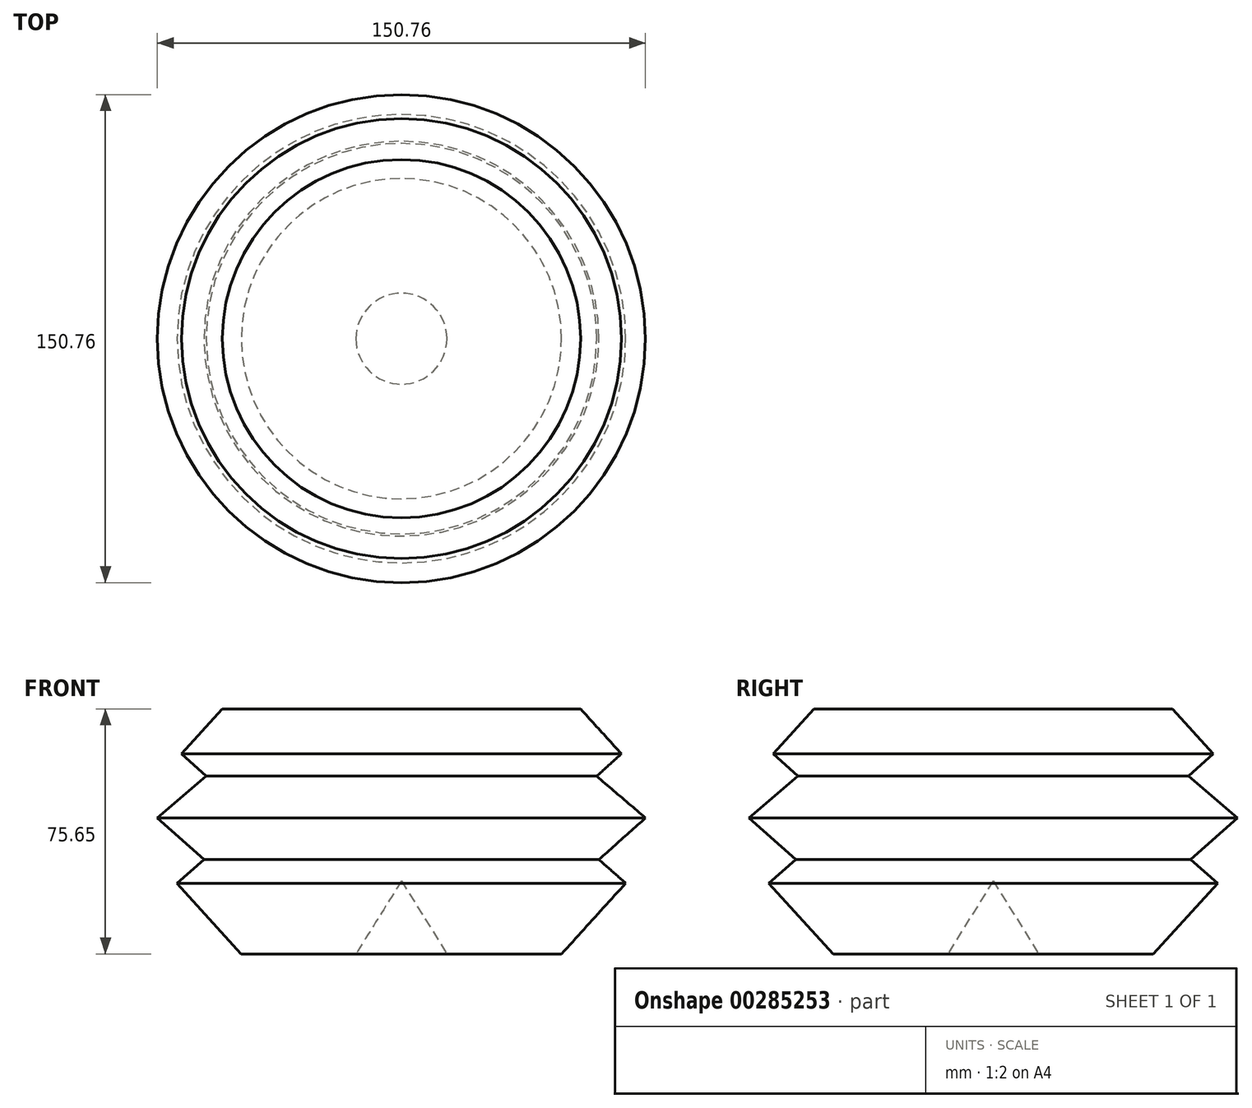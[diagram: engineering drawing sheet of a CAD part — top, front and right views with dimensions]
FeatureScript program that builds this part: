
annotation { "Feature Type Name" : "Feature", "Feature Type Description" : "" }
export const myFeature = defineFeature(function(context is Context, id is Id, definition is map)
    precondition{}
    {
        {
            var Q0;
            Q0=qCreatedBy(makeId("Front.planeOp"),FACE);
            var sketch = newSketch(context, id + "F0", { "sketchPlane" : qUnion([Q0])});
            skLineSegment(sketch, "E0", {"start": v(0, 22.53) * mm, "end": v(-14.06, 0) * mm});
            skLineSegment(sketch, "E1", {"start": v(-49.46, 0) * mm, "end": v(-14.06, 0) * mm});
            skLineSegment(sketch, "E2", {"start": v(-69.28, 21.85) * mm, "end": v(-49.46, 0) * mm});
            skLineSegment(sketch, "E3", {"start": v(-60.98, 29.13) * mm, "end": v(-69.28, 21.85) * mm});
            skLineSegment(sketch, "E4", {"start": v(-75.38, 42) * mm, "end": v(-60.98, 29.13) * mm});
            skLineSegment(sketch, "E5", {"start": v(-60.3, 54.88) * mm, "end": v(-75.38, 42) * mm});
            skLineSegment(sketch, "E6", {"start": v(-67.92, 61.83) * mm, "end": v(-60.3, 54.88) * mm});
            skLineSegment(sketch, "E7", {"start": v(-67.92, 61.83) * mm, "end": v(-55.33, 75.65) * mm});
            skLineSegment(sketch, "E8", {"start": v(-55.33, 75.65) * mm, "end": v(0, 75.65) * mm});
            skLineSegment(sketch, "E9", {"start": v(0, 75.65) * mm, "end": v(0, 22.53) * mm});
            skSolve(sketch);
        }
        {
            var Q0;
            Q0 = qSketchRegion(id + "F0", true);
            var Q1;
            Q1=sQuery(id+"F0.wireOp",EDGE,"E9");
            revolve(context, id + "F1", {"entities" : qUnion([Q0]), "axis" : qUnion([Q1]), "revolveType" : RevolveType.FULL});
        }
    });
